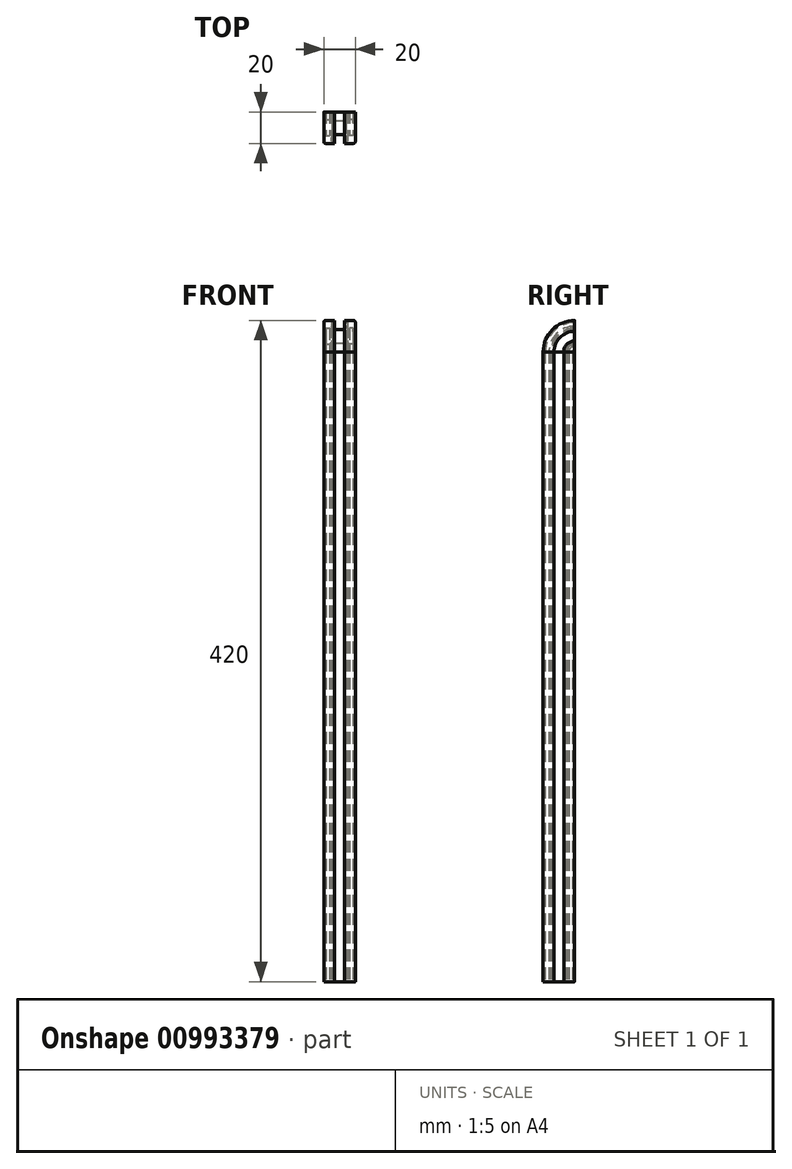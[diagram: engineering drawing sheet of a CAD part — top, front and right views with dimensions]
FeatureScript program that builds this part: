
annotation { "Feature Type Name" : "Feature", "Feature Type Description" : "" }
export const myFeature = defineFeature(function(context is Context, id is Id, definition is map)
    precondition{}
    {
        {
            var Q0;
            Q0=qCreatedBy(makeId("Top.planeOp"),FACE);
            var sketch = newSketch(context, id + "F0", { "sketchPlane" : qUnion([Q0])});
            skLineSegment(sketch, "E0.1", {"start": v(5.65, 6.9) * mm, "end": v(5.65, 13.1) * mm});
            skLineSegment(sketch, "E0.2", {"start": v(6.9, 5.65) * mm, "end": v(13.1, 5.65) * mm});
            skLineSegment(sketch, "E0.3", {"start": v(14.35, 6.9) * mm, "end": v(14.35, 13.1) * mm});
            skLineSegment(sketch, "E1", {"start": v(1, 20) * mm, "end": v(6.9, 20) * mm});
            skLineSegment(sketch, "E2", {"start": v(6.9, 20) * mm, "end": v(6.9, 18.7) * mm});
            skLineSegment(sketch, "E3", {"start": v(6.9, 18.7) * mm, "end": v(4.9, 18.7) * mm});
            skLineSegment(sketch, "E4", {"start": v(6.9, 14.35) * mm, "end": v(4.9, 16.35) * mm});
            skLineSegment(sketch, "E5", {"start": v(4.9, 18.7) * mm, "end": v(4.9, 16.35) * mm});
            skLineSegment(sketch, "E6.MirrorCS", {"start": v(0, 13.1) * mm, "end": v(1.3, 13.1) * mm});
            skLineSegment(sketch, "E7.MirrorCS", {"start": v(1.3, 13.1) * mm, "end": v(1.3, 15.1) * mm});
            skLineSegment(sketch, "E8.MirrorCS", {"start": v(1.3, 15.1) * mm, "end": v(3.65, 15.1) * mm});
            skLineSegment(sketch, "E9.MirrorCS", {"start": v(5.65, 13.1) * mm, "end": v(3.65, 15.1) * mm});
            skLineSegment(sketch, "E10", {"start": v(0, 19) * mm, "end": v(0, 13.1) * mm});
            skLineSegment(sketch, "E11.MirrorCS", {"start": v(13.1, 14.35) * mm, "end": v(15.1, 16.35) * mm});
            skLineSegment(sketch, "E12.MirrorCS", {"start": v(13.1, 18.7) * mm, "end": v(15.1, 18.7) * mm});
            skLineSegment(sketch, "E13.MirrorCS", {"start": v(13.1, 20) * mm, "end": v(13.1, 18.7) * mm});
            skLineSegment(sketch, "E14.MirrorCS", {"start": v(15.1, 18.7) * mm, "end": v(15.1, 16.35) * mm});
            skLineSegment(sketch, "E15.MirrorCS", {"start": v(14.35, 13.1) * mm, "end": v(16.35, 15.1) * mm});
            skLineSegment(sketch, "E16.MirrorCS", {"start": v(18.7, 15.1) * mm, "end": v(16.35, 15.1) * mm});
            skLineSegment(sketch, "E17.MirrorCS", {"start": v(18.7, 13.1) * mm, "end": v(18.7, 15.1) * mm});
            skLineSegment(sketch, "E18.MirrorCS", {"start": v(20, 13.1) * mm, "end": v(18.7, 13.1) * mm});
            skLineSegment(sketch, "E19.MirrorCS", {"start": v(20, 19) * mm, "end": v(20, 13.1) * mm});
            skLineSegment(sketch, "E20.MirrorCS", {"start": v(19, 20) * mm, "end": v(13.1, 20) * mm});
            skLineSegment(sketch, "E21.MirrorCS", {"start": v(0, 6.9) * mm, "end": v(1.3, 6.9) * mm});
            skLineSegment(sketch, "E22.MirrorCS", {"start": v(4.9, 1.3) * mm, "end": v(4.9, 3.65) * mm});
            skLineSegment(sketch, "E23.MirrorCS", {"start": v(1.3, 4.9) * mm, "end": v(3.65, 4.9) * mm});
            skLineSegment(sketch, "E24.MirrorCS", {"start": v(1.3, 6.9) * mm, "end": v(1.3, 4.9) * mm});
            skLineSegment(sketch, "E25.MirrorCS", {"start": v(5.65, 6.9) * mm, "end": v(3.65, 4.9) * mm});
            skLineSegment(sketch, "E26.MirrorCS", {"start": v(6.9, 5.65) * mm, "end": v(4.9, 3.65) * mm});
            skLineSegment(sketch, "E27.MirrorCS", {"start": v(6.9, 0) * mm, "end": v(6.9, 1.3) * mm});
            skLineSegment(sketch, "E28.MirrorCS", {"start": v(6.9, 1.3) * mm, "end": v(4.9, 1.3) * mm});
            skLineSegment(sketch, "E29.MirrorCS", {"start": v(18.7, 4.9) * mm, "end": v(16.35, 4.9) * mm});
            skLineSegment(sketch, "E30.MirrorCS", {"start": v(20, 6.9) * mm, "end": v(18.7, 6.9) * mm});
            skLineSegment(sketch, "E31.MirrorCS", {"start": v(15.1, 1.3) * mm, "end": v(15.1, 3.65) * mm});
            skLineSegment(sketch, "E32.MirrorCS", {"start": v(13.1, 0) * mm, "end": v(13.1, 1.3) * mm});
            skLineSegment(sketch, "E33.MirrorCS", {"start": v(13.1, 1.3) * mm, "end": v(15.1, 1.3) * mm});
            skLineSegment(sketch, "E34.MirrorCS", {"start": v(18.7, 6.9) * mm, "end": v(18.7, 4.9) * mm});
            skLineSegment(sketch, "E35.MirrorCS", {"start": v(19, 0) * mm, "end": v(13.1, 0) * mm});
            skLineSegment(sketch, "E36.MirrorCS", {"start": v(13.1, 5.65) * mm, "end": v(15.1, 3.65) * mm});
            skLineSegment(sketch, "E37.MirrorCS", {"start": v(20, 1) * mm, "end": v(20, 6.9) * mm});
            skLineSegment(sketch, "E38.MirrorCS", {"start": v(14.35, 6.9) * mm, "end": v(16.35, 4.9) * mm});
            skLineSegment(sketch, "E39", {"start": v(6.9, 14.35) * mm, "end": v(13.1, 14.35) * mm});
            skLineSegment(sketch, "E40", {"start": v(0, 6.9) * mm, "end": v(0, 1) * mm});
            skLineSegment(sketch, "E41", {"start": v(1, 0) * mm, "end": v(6.9, 0) * mm});
            skPoint(sketch, "E42.visualSharp", {"position": v(0, 20) * mm});
            skArc(sketch, "E42.filletArc", {"start": v(1, 20) * mm, "mid": v(0.3, 19.7) * mm, "end": v(0, 19) * mm});
            skPoint(sketch, "E43.visualSharp", {"position": v(20, 20) * mm});
            skArc(sketch, "E43.filletArc", {"start": v(20, 19) * mm, "mid": v(19.7, 19.7) * mm, "end": v(19, 20) * mm});
            skPoint(sketch, "E44.visualSharp", {"position": v(20, 0) * mm});
            skArc(sketch, "E44.filletArc", {"start": v(19, 0) * mm, "mid": v(19.7, 0.3) * mm, "end": v(20, 1) * mm});
            skPoint(sketch, "E45.visualSharp", {"position": v(0, 0) * mm});
            skArc(sketch, "E45.filletArc", {"start": v(0, 1) * mm, "mid": v(0.3, 0.3) * mm, "end": v(1, 0) * mm});
            skSolve(sketch);
        }
        {
            var Q0;
            Q0=qSketchRegion(id+"F0",true);
            extrude(context, id + "F1", {"entities" : qUnion([Q0]), "depth" : 400 * mm, "offsetDistance" : 25 * mm});
        }
        {
            var Q0;
            Q0=makeQuery(id+"F1.opExtrude","CAP_FACE",FACE,{"disambiguationData":[OSD([sQuery(id+"F0.wireOp",EDGE,"E0.1"),sQuery(id+"F0.wireOp",EDGE,"E0.2"),sQuery(id+"F0.wireOp",EDGE,"E0.3"),sQuery(id+"F0.wireOp",EDGE,"E1"),sQuery(id+"F0.wireOp",EDGE,"E2"),sQuery(id+"F0.wireOp",EDGE,"E3"),sQuery(id+"F0.wireOp",EDGE,"E4"),sQuery(id+"F0.wireOp",EDGE,"E5"),sQuery(id+"F0.wireOp",EDGE,"E6.MirrorCS"),sQuery(id+"F0.wireOp",EDGE,"E7.MirrorCS"),sQuery(id+"F0.wireOp",EDGE,"E8.MirrorCS"),sQuery(id+"F0.wireOp",EDGE,"E9.MirrorCS"),sQuery(id+"F0.wireOp",EDGE,"E10"),sQuery(id+"F0.wireOp",EDGE,"E11.MirrorCS"),sQuery(id+"F0.wireOp",EDGE,"E12.MirrorCS"),sQuery(id+"F0.wireOp",EDGE,"E13.MirrorCS"),sQuery(id+"F0.wireOp",EDGE,"E14.MirrorCS"),sQuery(id+"F0.wireOp",EDGE,"E15.MirrorCS"),sQuery(id+"F0.wireOp",EDGE,"E16.MirrorCS"),sQuery(id+"F0.wireOp",EDGE,"E17.MirrorCS"),sQuery(id+"F0.wireOp",EDGE,"E18.MirrorCS"),sQuery(id+"F0.wireOp",EDGE,"E19.MirrorCS"),sQuery(id+"F0.wireOp",EDGE,"E20.MirrorCS"),sQuery(id+"F0.wireOp",EDGE,"E21.MirrorCS"),sQuery(id+"F0.wireOp",EDGE,"E22.MirrorCS"),sQuery(id+"F0.wireOp",EDGE,"E23.MirrorCS"),sQuery(id+"F0.wireOp",EDGE,"E24.MirrorCS"),sQuery(id+"F0.wireOp",EDGE,"E25.MirrorCS"),sQuery(id+"F0.wireOp",EDGE,"E26.MirrorCS"),sQuery(id+"F0.wireOp",EDGE,"E27.MirrorCS"),sQuery(id+"F0.wireOp",EDGE,"E28.MirrorCS"),sQuery(id+"F0.wireOp",EDGE,"E29.MirrorCS"),sQuery(id+"F0.wireOp",EDGE,"E30.MirrorCS"),sQuery(id+"F0.wireOp",EDGE,"E31.MirrorCS"),sQuery(id+"F0.wireOp",EDGE,"E32.MirrorCS"),sQuery(id+"F0.wireOp",EDGE,"E33.MirrorCS"),sQuery(id+"F0.wireOp",EDGE,"E34.MirrorCS"),sQuery(id+"F0.wireOp",EDGE,"E35.MirrorCS"),sQuery(id+"F0.wireOp",EDGE,"E36.MirrorCS"),sQuery(id+"F0.wireOp",EDGE,"E37.MirrorCS"),sQuery(id+"F0.wireOp",EDGE,"E38.MirrorCS"),sQuery(id+"F0.wireOp",EDGE,"E39"),sQuery(id+"F0.wireOp",EDGE,"E40"),sQuery(id+"F0.wireOp",EDGE,"E41"),sQuery(id+"F0.wireOp",EDGE,"E42.filletArc"),sQuery(id+"F0.wireOp",EDGE,"E43.filletArc"),sQuery(id+"F0.wireOp",EDGE,"E44.filletArc"),sQuery(id+"F0.wireOp",EDGE,"E45.filletArc")])],"isStart":false});
            var sketch = newSketch(context, id + "F2", { "sketchPlane" : qUnion([Q0])});
            skLineSegment(sketch, "E46.0", {"start": v(20, 19) * mm, "end": v(20, 13.1) * mm});
            skLineSegment(sketch, "E47.0", {"start": v(20, 13.1) * mm, "end": v(18.7, 13.1) * mm});
            skLineSegment(sketch, "E48.0", {"start": v(18.7, 13.1) * mm, "end": v(18.7, 15.1) * mm});
            skLineSegment(sketch, "E49.0", {"start": v(18.7, 15.1) * mm, "end": v(16.35, 15.1) * mm});
            skLineSegment(sketch, "E50.0", {"start": v(14.35, 13.1) * mm, "end": v(16.35, 15.1) * mm});
            skLineSegment(sketch, "E51.0", {"start": v(14.35, 6.9) * mm, "end": v(14.35, 13.1) * mm});
            skLineSegment(sketch, "E52.0", {"start": v(14.35, 6.9) * mm, "end": v(16.35, 4.9) * mm});
            skLineSegment(sketch, "E53.0", {"start": v(18.7, 4.9) * mm, "end": v(16.35, 4.9) * mm});
            skLineSegment(sketch, "E54.0", {"start": v(18.7, 6.9) * mm, "end": v(18.7, 4.9) * mm});
            skLineSegment(sketch, "E54.1", {"start": v(20, 6.9) * mm, "end": v(18.7, 6.9) * mm});
            skLineSegment(sketch, "E54.2", {"start": v(20, 1) * mm, "end": v(20, 6.9) * mm});
            skLineSegment(sketch, "E54.3", {"start": v(15.1, 1.3) * mm, "end": v(15.1, 3.65) * mm});
            skLineSegment(sketch, "E54.4", {"start": v(13.1, 5.65) * mm, "end": v(15.1, 3.65) * mm});
            skArc(sketch, "E55.0", {"start": v(19, 0) * mm, "mid": v(19.7, 0.3) * mm, "end": v(20, 1) * mm});
            skLineSegment(sketch, "E55.1", {"start": v(19, 0) * mm, "end": v(13.1, 0) * mm});
            skLineSegment(sketch, "E55.2", {"start": v(13.1, 1.3) * mm, "end": v(15.1, 1.3) * mm});
            skPoint(sketch, "E55.3", {"position": v(13.1, 0.65) * mm});
            skArc(sketch, "E56.0", {"start": v(20, 19) * mm, "mid": v(19.7, 19.7) * mm, "end": v(19, 20) * mm});
            skLineSegment(sketch, "E56.1", {"start": v(19, 20) * mm, "end": v(13.1, 20) * mm});
            skLineSegment(sketch, "E56.2", {"start": v(13.1, 20) * mm, "end": v(13.1, 18.7) * mm});
            skLineSegment(sketch, "E56.3", {"start": v(13.1, 18.7) * mm, "end": v(15.1, 18.7) * mm});
            skLineSegment(sketch, "E56.4", {"start": v(15.1, 18.7) * mm, "end": v(15.1, 16.35) * mm});
            skLineSegment(sketch, "E56.5", {"start": v(13.1, 14.35) * mm, "end": v(15.1, 16.35) * mm});
            skLineSegment(sketch, "E56.6", {"start": v(19, 20) * mm, "end": v(13.1, 20) * mm});
            skLineSegment(sketch, "E56.7", {"start": v(15.1, 18.7) * mm, "end": v(15.1, 16.35) * mm});
            skPoint(sketch, "E56.8", {"position": v(13.1, 19.35) * mm});
            skLineSegment(sketch, "E57.0", {"start": v(6.9, 14.35) * mm, "end": v(13.1, 14.35) * mm});
            skLineSegment(sketch, "E57.1", {"start": v(6.9, 14.35) * mm, "end": v(4.9, 16.35) * mm});
            skLineSegment(sketch, "E57.2", {"start": v(4.9, 18.7) * mm, "end": v(4.9, 16.35) * mm});
            skLineSegment(sketch, "E57.3", {"start": v(6.9, 20) * mm, "end": v(6.9, 18.7) * mm});
            skLineSegment(sketch, "E57.4", {"start": v(1, 20) * mm, "end": v(6.9, 20) * mm});
            skLineSegment(sketch, "E57.5", {"start": v(5.65, 13.1) * mm, "end": v(3.65, 15.1) * mm});
            skLineSegment(sketch, "E57.6", {"start": v(5.65, 6.9) * mm, "end": v(5.65, 13.1) * mm});
            skLineSegment(sketch, "E57.7", {"start": v(5.65, 6.9) * mm, "end": v(3.65, 4.9) * mm});
            skLineSegment(sketch, "E57.8", {"start": v(1.3, 4.9) * mm, "end": v(3.65, 4.9) * mm});
            skLineSegment(sketch, "E57.9", {"start": v(1.3, 6.9) * mm, "end": v(1.3, 4.9) * mm});
            skPoint(sketch, "E57.10", {"position": v(4.9, 17.52) * mm});
            skPoint(sketch, "E57.11", {"position": v(4.65, 5.9) * mm});
            skSolve(sketch);
        }
        {
            var Q0;
            Q0=makeQuery(id+"F2.imprint","IMPRINT",FACE,{"disambiguationData":[TD([[makeQuery(id+"F2.imprint","IMPRINT",EDGE,{"derivedFrom":sQuery(id+"F2.wireOp",EDGE,"E46.0")}),-1.0]])]});
            var Q1;
            Q1=sQuery(id+"F2.wireOp",EDGE,"E56.1");
            revolve(context, id + "F3", {"surfaceOperationType" : NewSurfaceOperationType.NEW, "entities" : qUnion([Q0]), "axis" : qUnion([Q1]), "revolveType" : RevolveType.ONE_DIRECTION, "angle" : 90 * degree});
        }
    });
